annotation { "Feature Type Name" : "Feature", "Feature Type Description" : "" }
export const myFeature = defineFeature(function(context is Context, id is Id, definition is map)
    precondition{}
    {
        {
            var Q0;
            Q0=qCreatedBy(makeId("Top.planeOp"),FACE);
            var sketch = newSketch(context, id + "F0", { "sketchPlane" : qUnion([Q0])});
            skLineSegment(sketch, "E0.bottom", {"start": v(-107.95, 127) * mm, "end": v(107.95, 127) * mm});
            skLineSegment(sketch, "E0.top", {"start": v(-107.95, -127) * mm, "end": v(107.95, -127) * mm});
            skLineSegment(sketch, "E0.left", {"start": v(-107.95, 127) * mm, "end": v(-107.95, -127) * mm});
            skLineSegment(sketch, "E0.right", {"start": v(107.95, 127) * mm, "end": v(107.95, -127) * mm});
            skLineSegment(sketch, "E1", {"start": v(0, 127) * mm, "end": v(0, -127) * mm, "construction": true});
            skLineSegment(sketch, "E2", {"start": v(-107.95, 0) * mm, "end": v(107.95, 0) * mm, "construction": true});
            skPoint(sketch, "E3", {"position": v(0, 0) * mm});
            skSolve(sketch);
        }
        {
            var Q0;
            Q0 = qSketchRegion(id + "F0", true);
            extrude(context, id + "F1", {"entities" : qUnion([Q0]), "depth" : 12.7 * mm});
        }
        {
            var Q0;
            Q0=makeQuery(id+"F1.opExtrude","CAP_FACE",FACE,{"disambiguationData":[OSD([sQuery(id+"F0.wireOp",EDGE,"E0.bottom"),sQuery(id+"F0.wireOp",EDGE,"E0.top"),sQuery(id+"F0.wireOp",EDGE,"E0.left"),sQuery(id+"F0.wireOp",EDGE,"E0.right")])],"isStart":false});
            var sketch = newSketch(context, id + "F2", { "sketchPlane" : qUnion([Q0])});
            skLineSegment(sketch, "E4", {"start": v(-107.95, 68.83) * mm, "end": v(107.95, 68.83) * mm, "construction": true});
            skText(sketch, "E5", { "text": "VELCRO LOOP", "fontName": "RobotoSlab-Bold.ttf"});
            const initialGuessF2  = {"E5": [-0.10795, -0.09807, 1, 0, 0.02247]};
            skSetInitialGuess(sketch, initialGuessF2);
            skSolve(sketch);
        }
        {
            var Q0;
            Q0=makeQuery(id+"F2.imprint","IMPRINT",FACE,{"disambiguationData":[TD([[makeQuery(id+"F2.imprint","IMPRINT",EDGE,{"derivedFrom":sQuery(id+"F2.wireOp",EDGE,"E5.sketch_text.stroke-0")}),1.0]])]});
            var sketch = newSketch(context, id + "F3", { "sketchPlane" : qUnion([Q0])});
            skLineSegment(sketch, "E6.bottom", {"start": v(107.95, 127) * mm, "end": v(31.75, 127) * mm});
            skLineSegment(sketch, "E6.top", {"start": v(107.95, 25.4) * mm, "end": v(31.75, 25.4) * mm});
            skLineSegment(sketch, "E6.left", {"start": v(107.95, 127) * mm, "end": v(107.95, 25.4) * mm});
            skLineSegment(sketch, "E6.right", {"start": v(31.75, 127) * mm, "end": v(31.75, 25.4) * mm});
            skLineSegment(sketch, "E7.bottom", {"start": v(107.95, -127) * mm, "end": v(31.75, -127) * mm});
            skLineSegment(sketch, "E7.top", {"start": v(107.95, -63.5) * mm, "end": v(31.75, -63.5) * mm});
            skLineSegment(sketch, "E7.left", {"start": v(107.95, -127) * mm, "end": v(107.95, -63.5) * mm});
            skLineSegment(sketch, "E7.right", {"start": v(31.75, -127) * mm, "end": v(31.75, -63.5) * mm});
            skSolve(sketch);
        }
        {
            var Q0;
            Q0 = qSketchRegion(id + "F3", true);
            extrude(context, id + "F4", {"entities" : qUnion([Q0]), "operationType" : NewBodyOperationType.REMOVE, "endBound" : BoundingType.THROUGH_ALL, "oppositeDirection" : true, "depth" : 25.4 * mm});
        }
    });